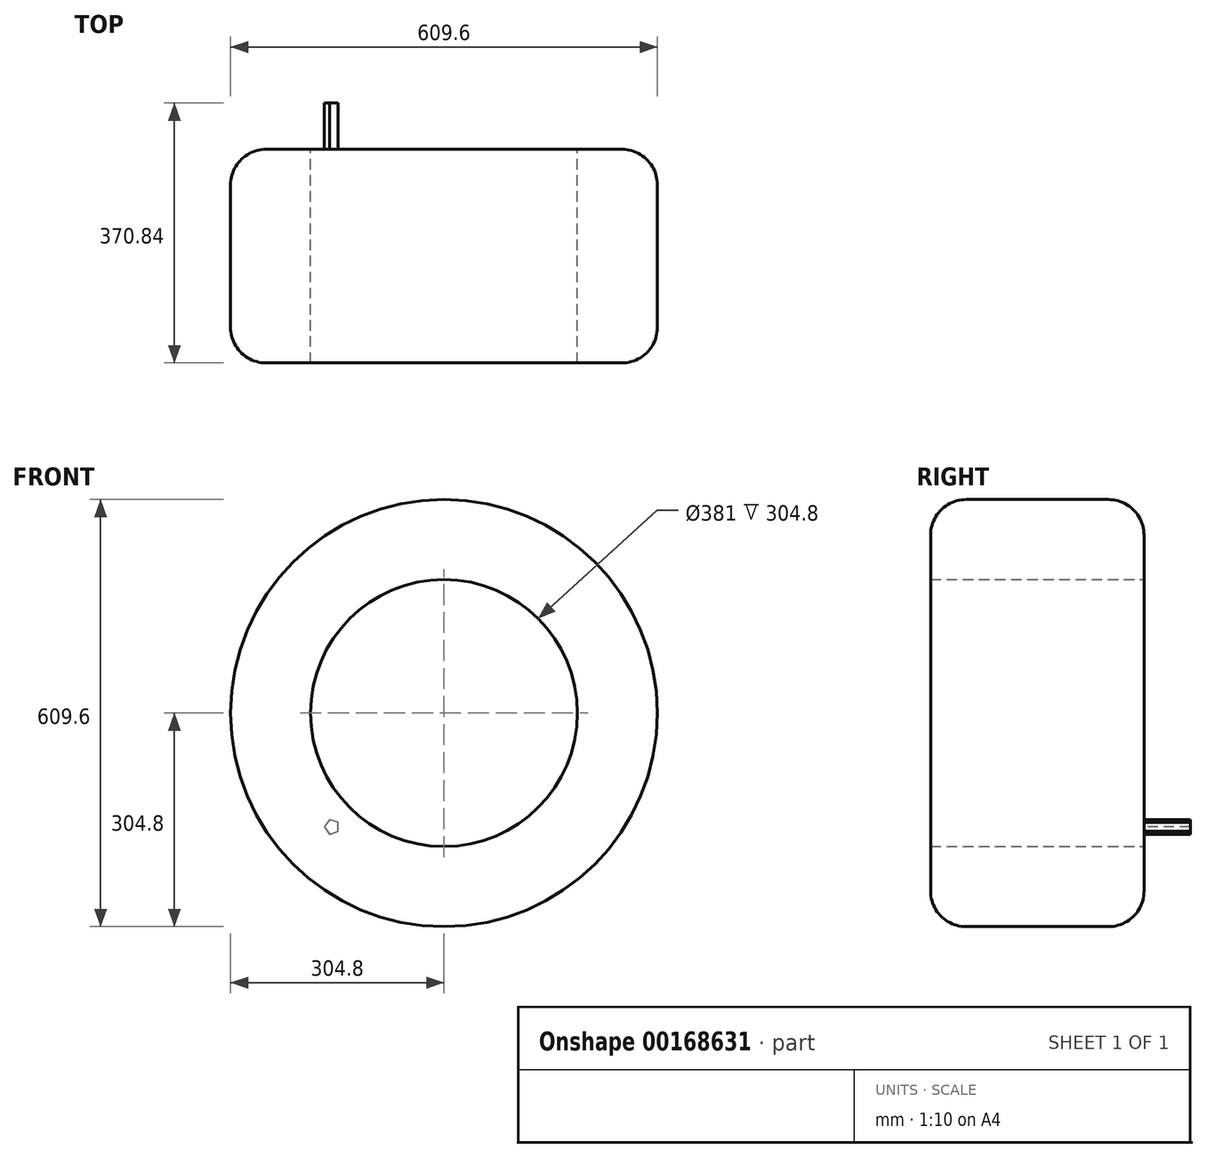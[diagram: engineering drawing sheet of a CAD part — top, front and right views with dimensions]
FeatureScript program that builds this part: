
annotation { "Feature Type Name" : "Feature", "Feature Type Description" : "" }
export const myFeature = defineFeature(function(context is Context, id is Id, definition is map)
    precondition{}
    {
        {
            var Q0;
            Q0=qCreatedBy(makeId("Front.planeOp"),FACE);
            var sketch = newSketch(context, id + "F0", { "sketchPlane" : qUnion([Q0])});
            skCircle(sketch, "E0", {"center": v(0, 0) * mm, "radius": 304.8 * mm});
            skSolve(sketch);
        }
        {
            var Q0;
            Q0 = qSketchRegion(id + "F0", true);
            extrude(context, id + "F1", {"entities" : qUnion([Q0]), "depth" : 304.8 * mm});
        }
        {
            var Q0;
            Q0=makeQuery(id+"F1.opExtrude","CAP_FACE",FACE,{"disambiguationData":[OSD([sQuery(id+"F0.wireOp",EDGE,"E0")])],"isStart":true});
            var sketch = newSketch(context, id + "F2", { "sketchPlane" : qUnion([Q0])});
            skCircle(sketch, "E1", {"center": v(0, 0) * mm, "radius": 190.5 * mm});
            skSolve(sketch);
        }
        {
            var Q0;
            Q0 = qSketchRegion(id + "F2", true);
            extrude(context, id + "F3", {"entities" : qUnion([Q0]), "operationType" : NewBodyOperationType.REMOVE, "oppositeDirection" : true, "depth" : 645.16 * mm});
        }
        {
            var Q0;
            Q0=makeQuery(id+"F1.opExtrude","CAP_EDGE",EDGE,{"disambiguationData":[OSD([sQuery(id+"F0.wireOp",EDGE,"E0")])],"isStart":false});
            var Q1;
            Q1=makeQuery(id+"F1.opExtrude","CAP_EDGE",EDGE,{"disambiguationData":[OSD([sQuery(id+"F0.wireOp",EDGE,"E0")])],"isStart":true});
            fillet(context, id + "F4", {"entities" : qUnion([Q0, Q1]), "radius" : 50.8 * mm, "tangentPropagation" : true, "allowEdgeOverflow" : false});
        }
        {
            var Q0;
            Q0=makeQuery(id+"F1.opExtrude","CAP_FACE",FACE,{"disambiguationData":[OSD([sQuery(id+"F0.wireOp",EDGE,"E0")])],"isStart":true});
            var sketch = newSketch(context, id + "F5", { "sketchPlane" : qUnion([Q0])});
            skCircle(sketch, "E2.cCircle", {"center": v(160.22, -162.62) * mm, "radius": 8.74 * mm, "construction": true});
            skLineSegment(sketch, "E2.0", {"start": v(151.48, -168.97) * mm, "end": v(151.48, -156.27) * mm});
            skLineSegment(sketch, "E2.1", {"start": v(151.48, -156.27) * mm, "end": v(163.56, -152.34) * mm});
            skLineSegment(sketch, "E2.2", {"start": v(163.56, -152.34) * mm, "end": v(171.02, -162.62) * mm});
            skLineSegment(sketch, "E2.3", {"start": v(171.02, -162.62) * mm, "end": v(163.56, -172.9) * mm});
            skLineSegment(sketch, "E2.4", {"start": v(163.56, -172.9) * mm, "end": v(151.48, -168.97) * mm});
            skPoint(sketch, "E2.0.midPoint", {"position": v(151.48, -162.62) * mm});
            skSolve(sketch);
        }
        {
            var Q0;
            Q0 = qSketchRegion(id + "F5", true);
            extrude(context, id + "F6", {"entities" : qUnion([Q0]), "operationType" : NewBodyOperationType.ADD, "depth" : 66.04 * mm});
        }
    });
